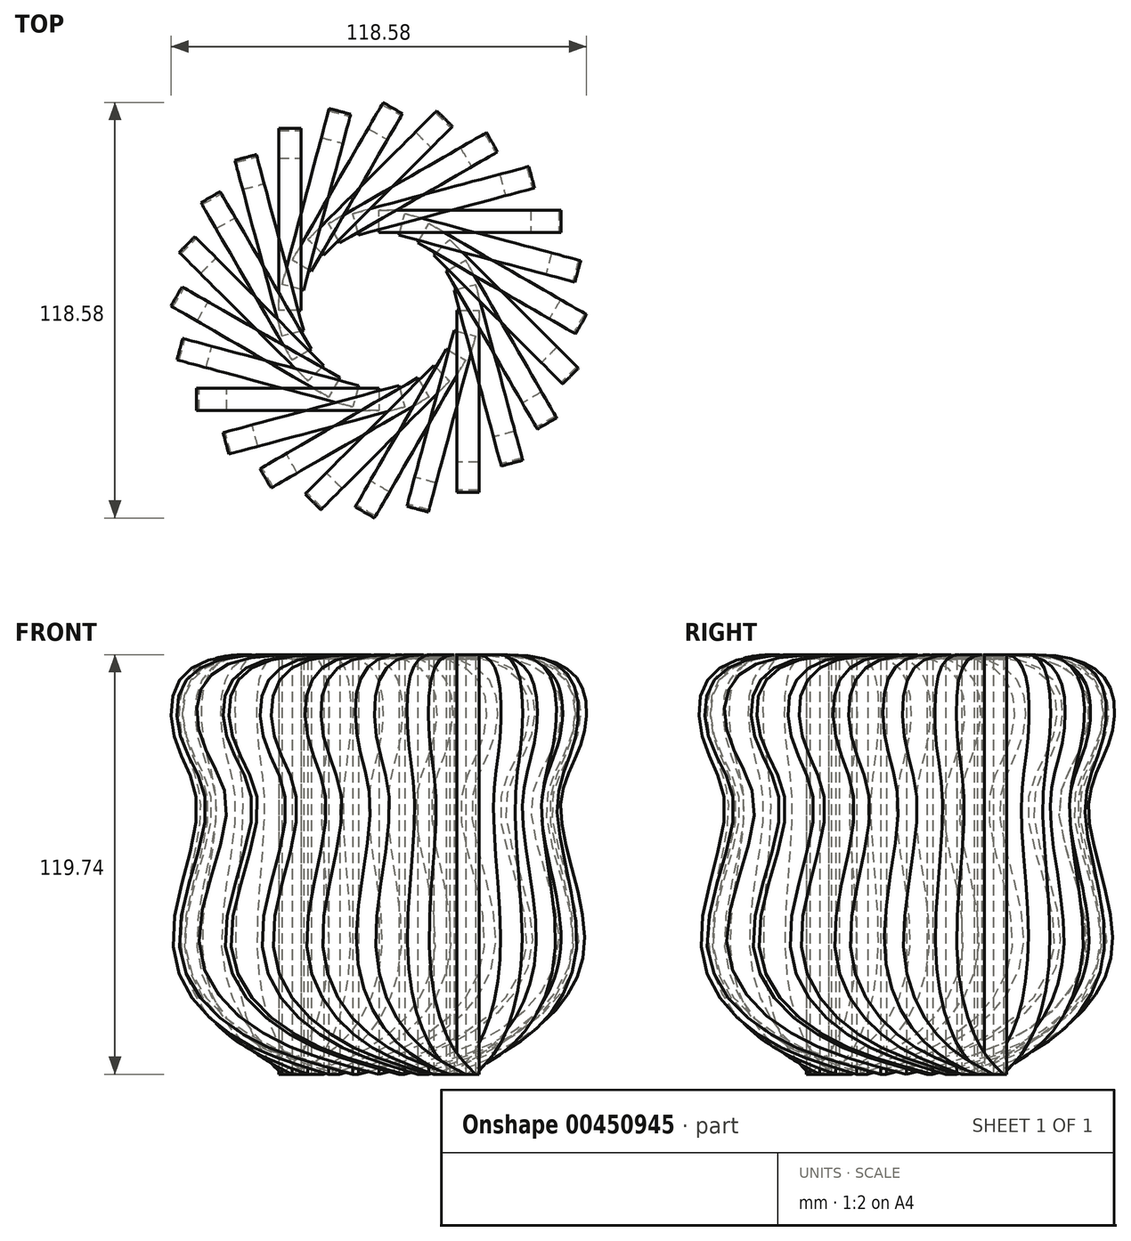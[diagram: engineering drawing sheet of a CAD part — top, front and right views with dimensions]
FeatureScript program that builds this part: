
annotation { "Feature Type Name" : "Feature", "Feature Type Description" : "" }
export const myFeature = defineFeature(function(context is Context, id is Id, definition is map)
    precondition{}
    {
        {
            var Q0;
            Q0=qCreatedBy(makeId("Front.planeOp"),FACE);
            var sketch = newSketch(context, id + "F0", { "sketchPlane" : qUnion([Q0])});
            skLineSegment(sketch, "E0", {"start": v(0, 0) * mm, "end": v(0, -118.43) * mm});
            skFitSpline(sketch, "E1", {"points": [v(0, 0) * mm, v(38.56, 0) * mm, v(50.6, -8.26) * mm, v(50.26, -23.75) * mm, v(43.38, -42.35) * mm, v(51.3, -80.9) * mm, v(34.08, -106.04) * mm, v(0, -118.43) * mm], "startDerivative": vector(252.86, 19.8) * mm, "endDerivative": vector(-217, -55.14) * mm});
            skSolve(sketch);
        }
        {
            var Q0;
            Q0 = qSketchRegion(id + "F0", true);
            extrude(context, id + "F1", {"entities" : qUnion([Q0]), "depth" : 3.17 * mm, "hasSecondDirection" : true, "secondDirectionOppositeDirection" : true, "secondDirectionDepth" : 3.17 * mm});
        }
        {
            var Q0;
            Q0=qCreatedBy(makeId("Front.planeOp"),FACE);
            cPlane(context, id + "F2", {"entities" : qUnion([Q0]), "cplaneType" : CPlaneType.OFFSET, "offset" : 25.4 * mm, "width" : 152.4 * mm, "height" : 152.4 * mm});
        }
        {
            var Q0;
            Q0=qCreatedBy(id+"F2.planeOp",FACE);
            var sketch = newSketch(context, id + "F3", { "sketchPlane" : qUnion([Q0])});
            skLineSegment(sketch, "E2", {"start": v(0, 0) * mm, "end": v(0, 49.71) * mm, "construction": true});
            skSolve(sketch);
        }
        {
            var Q0;
            Q0=makeQuery(id+"F1.opExtrude","SWEPT_BODY",BODY,{"disambiguationData":[OSD([sQuery(id+"F0.wireOp",EDGE,"E0"),sQuery(id+"F0.wireOp",EDGE,"E1")])]});
            var Q1;
            Q1=sQuery(id+"F3.wireOp",EDGE,"E2");
            circularPattern(context, id + "F4", {"entities" : qUnion([Q0]), "axis" : qUnion([Q1]), "angle" : 360 * degree, "instanceCount" : 24, "equalSpace" : true});
        }
    });
